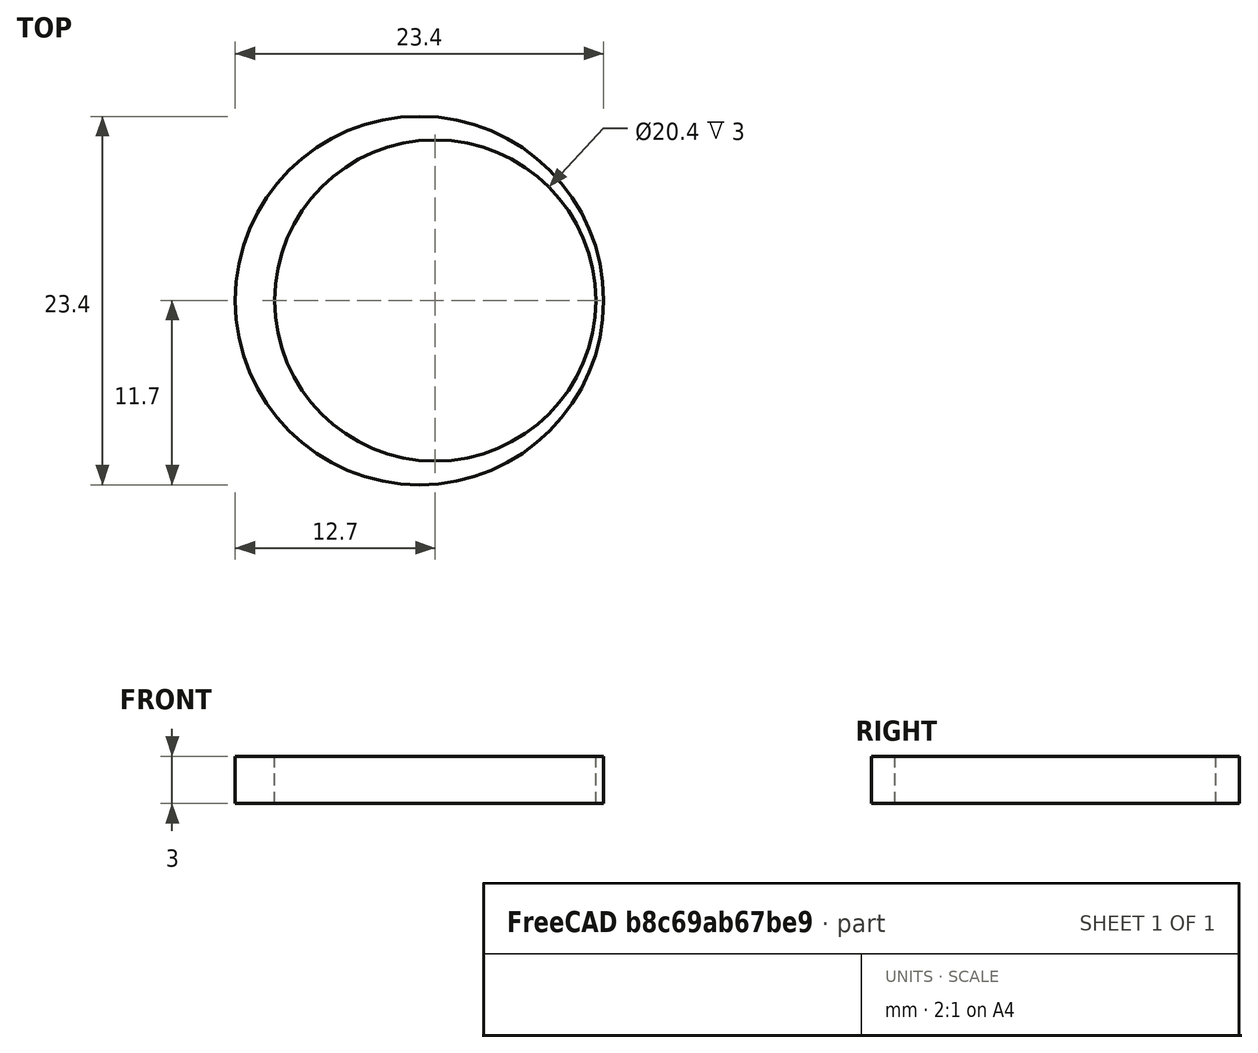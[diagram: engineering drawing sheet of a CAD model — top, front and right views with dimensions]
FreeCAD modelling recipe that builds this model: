
FCSTD DOCUMENT  (FreeCAD 0.19R23964 (Git))
Label: anillo
License: Creative Commons Attribution-ShareAlike
LicenseURL: http://creativecommons.org/licenses/by-sa/4.0/
objects: PartDesign::AdditiveCylinder×1, PartDesign::SubtractiveCylinder×1, PartDesign::Body×1
note: 5 computed .brp shape members not serialized (recipe doc carries the construction recipe); baked Part::Feature solids carry a one-line shape summary decoded from their .brp

FEATURE [PartDesign::AdditiveCylinder] Cylinder  label="Exterior"
  Angle = 360
  AttacherType = Attacher::AttachEngine3D
  Height = 3
  MapMode = 5
  Radius = 11.7
  Refine = true
  Support = -> [XY_Plane]
FEATURE [PartDesign::SubtractiveCylinder] Cylinder001  label="Interior"
  Angle = 360
  AttacherType = Attacher::AttachEngine3D
  BaseFeature = -> Cylinder
  Height = 3
  MapMode = 5
  Radius = 10.2
  Refine = true
  Support = -> [XY_Plane]
FEATURE [PartDesign::Body] Body  label="Anillo"
  Group = -> [Cylinder,Cylinder001]
  Origin = -> Origin
  Tip = -> Cylinder001
